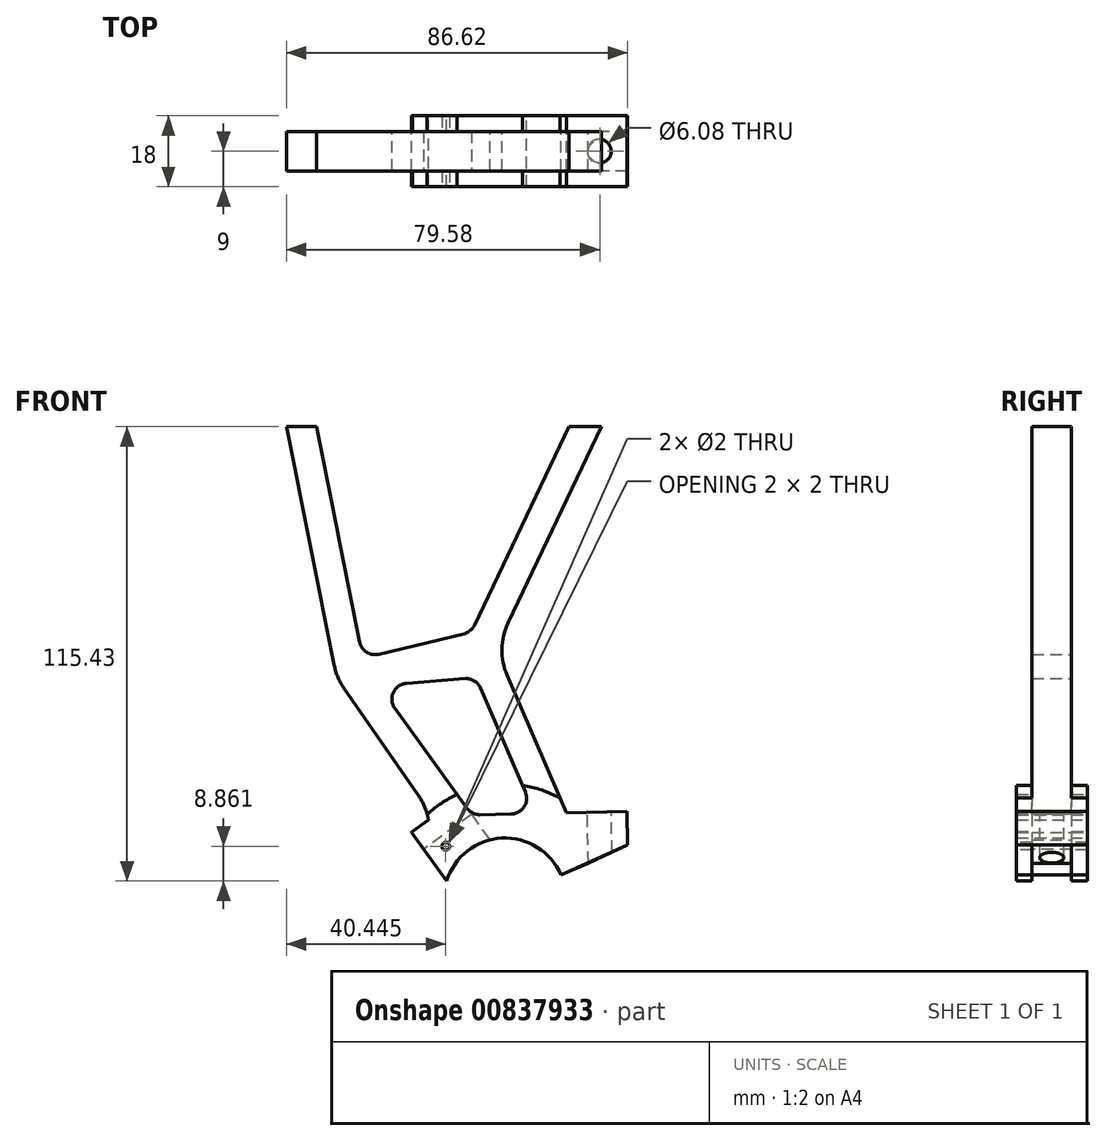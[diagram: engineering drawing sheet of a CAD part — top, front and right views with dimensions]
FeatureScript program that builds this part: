
annotation { "Feature Type Name" : "Feature", "Feature Type Description" : "" }
export const myFeature = defineFeature(function(context is Context, id is Id, definition is map)
    precondition{}
    {
        {
            var Q0;
            Q0=qCreatedBy(makeId("Front.planeOp"),FACE);
            var sketch = newSketch(context, id + "F0", { "sketchPlane" : qUnion([Q0])});
            skCircle(sketch, "E0", {"center": v(15.5, -66) * mm, "radius": 15.5 * mm});
            skLineSegment(sketch, "E1.bottom", {"start": v(-80, 54) * mm, "end": v(80, 54) * mm});
            skLineSegment(sketch, "E1.top", {"start": v(-80, 60) * mm, "end": v(80, 60) * mm});
            skLineSegment(sketch, "E1.left", {"start": v(-80, 54) * mm, "end": v(-80, 60) * mm});
            skLineSegment(sketch, "E1.right", {"start": v(80, 54) * mm, "end": v(80, 60) * mm});
            skLineSegment(sketch, "E2", {"start": v(-40, 54) * mm, "end": v(-27.92, -6.51) * mm});
            skCircle(sketch, "E3", {"center": v(15.5, -66) * mm, "radius": 23 * mm});
            skLineSegment(sketch, "E4", {"start": v(-25.36, -12.5) * mm, "end": v(-6.56, -39.57) * mm});
            skLineSegment(sketch, "E5", {"start": v(40, 54) * mm, "end": v(16.28, 4.1) * mm});
            skLineSegment(sketch, "E6", {"start": v(16.03, -9.1) * mm, "end": v(36.62, -56.9) * mm});
            skPoint(sketch, "E7.visualSharp", {"position": v(13.17, -2.45) * mm});
            skArc(sketch, "E7.filletArc", {"start": v(16.28, 4.1) * mm, "mid": v(14.73, -2.48) * mm, "end": v(16.03, -9.1) * mm});
            skPoint(sketch, "E8.visualSharp", {"position": v(-27.26, -9.77) * mm});
            skArc(sketch, "E8.filletArc", {"start": v(-27.92, -6.51) * mm, "mid": v(-26.95, -9.64) * mm, "end": v(-25.36, -12.5) * mm});
            skLineSegment(sketch, "E9", {"start": v(-16.58, -3.79) * mm, "end": v(5.05, 1.4) * mm});
            skLineSegment(sketch, "E10", {"start": v(-9.57, -11.2) * mm, "end": v(5.28, -9.99) * mm});
            skLineSegment(sketch, "E11", {"start": v(-32.35, 54) * mm, "end": v(-21.43, -0.68) * mm});
            skLineSegment(sketch, "E12", {"start": v(-12.49, -17.54) * mm, "end": v(5.82, -42.9) * mm});
            skLineSegment(sketch, "E13", {"start": v(31.7, 54) * mm, "end": v(7.73, 3.57) * mm});
            skLineSegment(sketch, "E14", {"start": v(9.28, -12.4) * mm, "end": v(20.66, -38.8) * mm});
            skArc(sketch, "E15.filletArc", {"start": v(-9.57, -11.2) * mm, "mid": v(-12.88, -13.52) * mm, "end": v(-12.49, -17.54) * mm});
            skArc(sketch, "E16.filletArc", {"start": v(9.28, -12.4) * mm, "mid": v(7.67, -10.55) * mm, "end": v(5.28, -9.99) * mm});
            skArc(sketch, "E17.filletArc", {"start": v(5.05, 1.4) * mm, "mid": v(6.63, 2.18) * mm, "end": v(7.73, 3.57) * mm});
            skArc(sketch, "E18.filletArc", {"start": v(-21.43, -0.68) * mm, "mid": v(-19.66, -3.27) * mm, "end": v(-16.58, -3.79) * mm});
            skLineSegment(sketch, "E19", {"start": v(9.15, -44.56) * mm, "end": v(17.08, -44.4) * mm});
            skPoint(sketch, "E20.visualSharp", {"position": v(7.05, -44.6) * mm});
            skArc(sketch, "E20.filletArc", {"start": v(5.82, -42.9) * mm, "mid": v(7.28, -44.15) * mm, "end": v(9.15, -44.56) * mm});
            skPoint(sketch, "E21.visualSharp", {"position": v(23.01, -44.26) * mm});
            skArc(sketch, "E21.filletArc", {"start": v(17.08, -44.4) * mm, "mid": v(20.36, -42.55) * mm, "end": v(20.66, -38.8) * mm});
            skLineSegment(sketch, "E22", {"start": v(2.52, -63.97) * mm, "end": v(-12.93, -42.55) * mm});
            skPoint(sketch, "E22.endSnap0", {"position": v(20.36, -42.55) * mm});
            skLineSegment(sketch, "E23", {"start": v(-8.28, -49) * mm, "end": v(3.89, -40.23) * mm});
            skLineSegment(sketch, "E24", {"start": v(-7.5, -66) * mm, "end": v(-4.16, -52.56) * mm});
            skPoint(sketch, "E25.newPointA", {"position": v(-2.2, -44.62) * mm});
            skPoint(sketch, "E25.newPointB", {"position": v(0, -49) * mm});
            skArc(sketch, "E25.filletArc", {"start": v(-4.16, -52.56) * mm, "mid": v(-3.96, -45.8) * mm, "end": v(-6.56, -39.57) * mm});
            skLineSegment(sketch, "E26", {"start": v(15.5, -66) * mm, "end": v(36.62, -56.9) * mm});
            skLineSegment(sketch, "E27", {"start": v(17.08, -44.4) * mm, "end": v(46.44, -43.75) * mm});
            skLineSegment(sketch, "E28", {"start": v(46.44, -43.75) * mm, "end": v(46.62, -52.29) * mm});
            skLineSegment(sketch, "E29", {"start": v(46.62, -52.29) * mm, "end": v(36.62, -56.9) * mm});
            skSolve(sketch);
        }
        {
            var Q0;
            {var subQ5=sQuery(id+"F0.wireOp",EDGE,"E2");Q0=makeQuery(id+"F0.imprint","IMPRINT",FACE,{"disambiguationData":[TD([[makeQuery(id+"F0.imprint","IMPRINT",EDGE,{"derivedFrom":subQ5}),1.0]])]});}
            var Q1;
            {var subQ9=sQuery(id+"F0.wireOp",EDGE,"E19");Q1=makeQuery(id+"F0.imprint","IMPRINT",FACE,{"disambiguationData":[TD([[makeQuery(id+"F0.imprint","IMPRINT",EDGE,{"derivedFrom":subQ9}),-1.0]])]});}
            var Q2;
            {var subQ3=sQuery(id+"F0.wireOp",EDGE,"E3");var subQ5=sQuery(id+"F0.wireOp",EDGE,"E20.filletArc");var subQ8=makeQuery(id+"F0.imprint","INTERSECT",VERTEX,{"derivedFrom":[subQ3,subQ5]});Q2=makeQuery(id+"F0.imprint","IMPRINT",FACE,{"disambiguationData":[TD([[makeQuery(id+"F0.imprint","IMPRINT",EDGE,{"disambiguationData":[TD([[subQ8,-1.0]])],"derivedFrom":subQ3}),-1.0]])]});}
            var Q3;
            {var subQ0=sQuery(id+"F0.wireOp",EDGE,"UMG4V04Q-lBuE-BQq7-RcGr-pR0ub9uLXrvf");Q3=makeQuery(id+"F0.imprint","IMPRINT",FACE,{"disambiguationData":[TD([[makeQuery(id+"F0.imprint","IMPRINT",EDGE,{"derivedFrom":subQ0}),1.0]])]});}
            var Q4;
            {var subQ0=sQuery(id+"F0.wireOp",EDGE,"E6");var subQ3=sQuery(id+"F0.wireOp",EDGE,"RwlM4oHN-kXNB-WGwk-zlGt-H1iUbLNf6ePu");var subQ5=makeQuery(id+"F0.imprint","INTERSECT",VERTEX,{"derivedFrom":[subQ0,subQ3]});Q4=makeQuery(id+"F0.imprint","IMPRINT",FACE,{"disambiguationData":[TD([[makeQuery(id+"F0.imprint","IMPRINT",EDGE,{"disambiguationData":[TD([[subQ5,-1.0]])],"derivedFrom":subQ3}),1.0]])]});}
            var Q5;
            {var subQ4=sQuery(id+"F0.wireOp",EDGE,"E28");Q5=makeQuery(id+"F0.imprint","IMPRINT",FACE,{"disambiguationData":[TD([[makeQuery(id+"F0.imprint","IMPRINT",EDGE,{"derivedFrom":subQ4}),-1.0]])]});}
            var Q6;
            {var subQ0=sQuery(id+"F0.wireOp",EDGE,"E6");var subQ3=sQuery(id+"F0.wireOp",EDGE,"E27");var subQ5=makeQuery(id+"F0.imprint","INTERSECT",VERTEX,{"derivedFrom":[subQ0,subQ3]});Q6=makeQuery(id+"F0.imprint","IMPRINT",FACE,{"disambiguationData":[TD([[makeQuery(id+"F0.imprint","IMPRINT",EDGE,{"disambiguationData":[TD([[subQ5,1.0]])],"derivedFrom":subQ3}),-1.0]])]});}
            var Q7;
            {var subQ0=sQuery(id+"F0.wireOp",EDGE,"E27");var subQ1=sQuery(id+"F0.wireOp",EDGE,"E3");var subQ2=makeQuery(id+"F0.imprint","INTERSECT",VERTEX,{"derivedFrom":[subQ1,subQ0]});Q7=makeQuery(id+"F0.imprint","IMPRINT",FACE,{"disambiguationData":[TD([[makeQuery(id+"F0.imprint","IMPRINT",EDGE,{"disambiguationData":[TD([[subQ2,-1.0]])],"derivedFrom":subQ1}),1.0]])]});}
            var Q8;
            {var subQ0=sQuery(id+"F0.wireOp",EDGE,"E23");var subQ1=sQuery(id+"F0.wireOp",EDGE,"E22");var subQ2=makeQuery(id+"F0.imprint","INTERSECT",VERTEX,{"derivedFrom":[subQ1,subQ0]});Q8=makeQuery(id+"F0.imprint","IMPRINT",FACE,{"disambiguationData":[TD([[makeQuery(id+"F0.imprint","IMPRINT",EDGE,{"disambiguationData":[TD([[subQ2,1.0]])],"derivedFrom":subQ1}),-1.0]])]});}
            extrude(context, id + "F1", {"entities" : qUnion([Q0, Q1, Q2, Q3, Q4, Q5, Q6, Q7, Q8]), "depth" : 10 * mm, "offsetDistance" : 25 * mm});
        }
        {
            var Q0;
            Q0=makeQuery(id+"F1.opExtrude","CAP_FACE",FACE,{"disambiguationData":[OSD([sQuery(id+"F0.wireOp",EDGE,"E0"),sQuery(id+"F0.wireOp",EDGE,"E1.bottom"),sQuery(id+"F0.wireOp",EDGE,"E2"),sQuery(id+"F0.wireOp",EDGE,"E4"),sQuery(id+"F0.wireOp",EDGE,"E5"),sQuery(id+"F0.wireOp",EDGE,"E6"),sQuery(id+"F0.wireOp",EDGE,"E7.filletArc"),sQuery(id+"F0.wireOp",EDGE,"E8.filletArc"),sQuery(id+"F0.wireOp",EDGE,"E9"),sQuery(id+"F0.wireOp",EDGE,"E10"),sQuery(id+"F0.wireOp",EDGE,"E11"),sQuery(id+"F0.wireOp",EDGE,"E12"),sQuery(id+"F0.wireOp",EDGE,"E13"),sQuery(id+"F0.wireOp",EDGE,"E14"),sQuery(id+"F0.wireOp",EDGE,"E15.filletArc"),sQuery(id+"F0.wireOp",EDGE,"E16.filletArc"),sQuery(id+"F0.wireOp",EDGE,"E17.filletArc"),sQuery(id+"F0.wireOp",EDGE,"E18.filletArc"),sQuery(id+"F0.wireOp",EDGE,"E19"),sQuery(id+"F0.wireOp",EDGE,"E20.filletArc"),sQuery(id+"F0.wireOp",EDGE,"E21.filletArc"),sQuery(id+"F0.wireOp",EDGE,"E22"),sQuery(id+"F0.wireOp",EDGE,"E24"),sQuery(id+"F0.wireOp",EDGE,"E25.filletArc"),sQuery(id+"F0.wireOp",EDGE,"E26"),sQuery(id+"F0.wireOp",EDGE,"UMG4V04Q-lBuE-BQq7-RcGr-pR0ub9uLXrvf"),sQuery(id+"F0.wireOp",EDGE,"0qV3wNh2-YUjg-HlTK-uqeD-eTxvEMBsVgpc"),sQuery(id+"F0.wireOp",EDGE,"RwlM4oHN-kXNB-WGwk-zlGt-H1iUbLNf6ePu")])],"isStart":false});
            var sketch = newSketch(context, id + "F2", { "sketchPlane" : qUnion([Q0])});
            skArc(sketch, "E30", {"start": v(29.74, -59.87) * mm, "mid": v(14.67, -50.52) * mm, "end": v(0.69, -61.43) * mm});
            skCircle(sketch, "E31", {"center": v(15.5, -66) * mm, "radius": 29.22 * mm});
            skLineSegment(sketch, "E32", {"start": v(0.69, -61.43) * mm, "end": v(-8.28, -49) * mm});
            skArc(sketch, "E33", {"start": v(-8.28, -49) * mm, "mid": v(-5.46, -44.65) * mm, "end": v(-6.56, -39.57) * mm});
            skLineSegment(sketch, "E34", {"start": v(5.82, -42.9) * mm, "end": v(0, -34.84) * mm});
            skLineSegment(sketch, "E35", {"start": v(0, -34.84) * mm, "end": v(-6.56, -39.57) * mm});
            skArc(sketch, "E36", {"start": v(5.82, -42.9) * mm, "mid": v(7.28, -44.15) * mm, "end": v(9.15, -44.56) * mm});
            skArc(sketch, "E37", {"start": v(0, -34.84) * mm, "mid": v(-5.6, -33.99) * mm, "end": v(-6.56, -39.57) * mm});
            skLineSegment(sketch, "E38", {"start": v(29.74, -59.87) * mm, "end": v(46.62, -52.29) * mm});
            skLineSegment(sketch, "E39", {"start": v(46.62, -52.29) * mm, "end": v(46.44, -43.75) * mm});
            skLineSegment(sketch, "E40", {"start": v(46.44, -43.75) * mm, "end": v(34.74, -44) * mm});
            skLineSegment(sketch, "E41", {"start": v(34.74, -44) * mm, "end": v(29.74, -59.87) * mm});
            skSolve(sketch);
        }
        {
            var Q0;
            Q0=makeQuery(id+"F2.imprint","IMPRINT",FACE,{"disambiguationData":[TD([[makeQuery(id+"F2.imprint","IMPRINT",EDGE,{"derivedFrom":sQuery(id+"F2.wireOp",EDGE,"E30")}),-1.0]])]});
            var Q1;
            {var subQ4=sQuery(id+"F2.wireOp",EDGE,"E39");Q1=makeQuery(id+"F2.imprint","IMPRINT",FACE,{"disambiguationData":[TD([[makeQuery(id+"F2.imprint","IMPRINT",EDGE,{"derivedFrom":subQ4}),-1.0]])]});}
            var Q2;
            {var subQ0=sQuery(id+"F2.wireOp",EDGE,"E41");Q2=makeQuery(id+"F2.imprint","IMPRINT",FACE,{"disambiguationData":[TD([[makeQuery(id+"F2.imprint","IMPRINT",EDGE,{"derivedFrom":subQ0}),1.0]])]});}
            extrude(context, id + "F3", {"entities" : qUnion([Q0, Q1, Q2]), "operationType" : NewBodyOperationType.ADD, "depth" : 4 * mm, "offsetDistance" : 25 * mm, "hasSecondDirection" : true, "secondDirectionOppositeDirection" : true, "secondDirectionDepth" : 14 * mm});
        }
        {
            var Q0;
            {var subQ0=sQuery(id+"F0.wireOp",EDGE,"E27");Q0=makeQuery(id+"F3.boolean.opBoolean","MERGE",FACE,{"derivedFrom":[makeQuery(id+"F1.opExtrude","SWEPT_FACE",FACE,{"disambiguationData":[OSD([subQ0])]}),makeQuery(id+"F3.opExtrude","SWEPT_FACE",FACE,{"disambiguationData":[OSD([subQ0,sQuery(id+"F2.wireOp",EDGE,"E40")])]})]});}
            var sketch = newSketch(context, id + "F4", { "sketchPlane" : qUnion([Q0])});
            skCircle(sketch, "E42", {"center": v(38.47, -5) * mm, "radius": 3.04 * mm});
            skSolve(sketch);
        }
        {
            var Q0;
            Q0=makeQuery(id+"F4.imprint","IMPRINT",FACE,{"disambiguationData":[TD([[makeQuery(id+"F4.imprint","IMPRINT",EDGE,{"derivedFrom":sQuery(id+"F4.wireOp",EDGE,"E42")}),1.0]])]});
            extrude(context, id + "F5", {"entities" : qUnion([Q0]), "operationType" : NewBodyOperationType.REMOVE, "oppositeDirection" : true, "depth" : 25 * mm, "offsetDistance" : 25 * mm});
        }
        {
            var Q0;
            Q0=makeQuery(id+"F3.boolean.opBoolean","MERGE",FACE,{"derivedFrom":[makeQuery(id+"F1.opExtrude","SWEPT_FACE",FACE,{"disambiguationData":[OSD([sQuery(id+"F0.wireOp",EDGE,"E22")])]}),makeQuery(id+"F3.opExtrude","SWEPT_FACE",FACE,{"disambiguationData":[OSD([sQuery(id+"F2.wireOp",EDGE,"E32")])]})]});
            var sketch = newSketch(context, id + "F6", { "sketchPlane" : qUnion([Q0])});
            skLineSegment(sketch, "E43.bottom", {"start": v(0, -34.9) * mm, "end": v(10, -34.9) * mm});
            skLineSegment(sketch, "E43.top", {"start": v(0, -50.22) * mm, "end": v(10, -50.22) * mm});
            skLineSegment(sketch, "E43.left", {"start": v(0, -34.9) * mm, "end": v(0, -50.22) * mm});
            skLineSegment(sketch, "E43.right", {"start": v(10, -34.9) * mm, "end": v(10, -50.22) * mm});
            skLineSegment(sketch, "E44.left", {"start": v(0, -50.22) * mm, "end": v(0, -50.22) * mm});
            skLineSegment(sketch, "E44.right", {"start": v(10, -50.22) * mm, "end": v(10, -50.22) * mm});
            skLineSegment(sketch, "E45.top", {"start": v(0, -40.22) * mm, "end": v(10, -40.22) * mm});
            skLineSegment(sketch, "E45.left", {"start": v(0, -50.22) * mm, "end": v(0, -40.22) * mm});
            skLineSegment(sketch, "E45.right", {"start": v(10, -50.22) * mm, "end": v(10, -40.22) * mm});
            skSolve(sketch);
        }
        {
            var Q0;
            Q0=makeQuery(id+"F6.imprint","IMPRINT",FACE,{"disambiguationData":[TD([[makeQuery(id+"F6.imprint","IMPRINT",EDGE,{"derivedFrom":sQuery(id+"F6.wireOp",EDGE,"E43.top")}),-1.0]])]});
            extrude(context, id + "F7", {"entities" : qUnion([Q0]), "operationType" : NewBodyOperationType.REMOVE, "oppositeDirection" : true, "depth" : 15 * mm, "offsetDistance" : 25 * mm});
        }
        {
            var Q0;
            Q0=makeQuery(id+"F3.opExtrude","CAP_FACE",FACE,{"disambiguationData":[OSD([sQuery(id+"F0.wireOp",EDGE,"E6"),sQuery(id+"F0.wireOp",EDGE,"E14"),sQuery(id+"F0.wireOp",EDGE,"E19"),sQuery(id+"F0.wireOp",EDGE,"E21.filletArc"),sQuery(id+"F0.wireOp",EDGE,"E23"),sQuery(id+"F0.wireOp",EDGE,"E25.filletArc"),sQuery(id+"F0.wireOp",EDGE,"E27"),sQuery(id+"F2.wireOp",EDGE,"E30"),sQuery(id+"F2.wireOp",EDGE,"E31"),sQuery(id+"F2.wireOp",EDGE,"E32"),sQuery(id+"F2.wireOp",EDGE,"E33"),sQuery(id+"F2.wireOp",EDGE,"E34"),sQuery(id+"F2.wireOp",EDGE,"E36"),sQuery(id+"F2.wireOp",EDGE,"E38"),sQuery(id+"F2.wireOp",EDGE,"E39"),sQuery(id+"F2.wireOp",EDGE,"E40")])],"isStart":false});
            var sketch = newSketch(context, id + "F8", { "sketchPlane" : qUnion([Q0])});
            skCircle(sketch, "E46", {"center": v(0.45, -52.57) * mm, "radius": 1 * mm});
            skSolve(sketch);
        }
        {
            var Q0;
            Q0=makeQuery(id+"F8.imprint","IMPRINT",FACE,{"disambiguationData":[TD([[makeQuery(id+"F8.imprint","IMPRINT",EDGE,{"derivedFrom":sQuery(id+"F8.wireOp",EDGE,"E46")}),1.0]])]});
            extrude(context, id + "F9", {"entities" : qUnion([Q0]), "operationType" : NewBodyOperationType.REMOVE, "oppositeDirection" : true, "depth" : 25 * mm, "offsetDistance" : 25 * mm});
        }
    });
